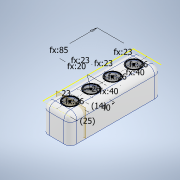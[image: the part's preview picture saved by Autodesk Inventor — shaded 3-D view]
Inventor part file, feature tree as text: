
AUTODESK INVENTOR PART (.ipt)
format: ipt  version: 2021 (Build 250183000, 183)  size: 2,222,592 bytes
history: native  units: in
note: dims shown in document units (in); Inventor stores cm internally (conversion verified against a paired STEP export)
features: extrude x9, other x9, fillet x2
ambient origin geometry x8: Origin, YZ Plane, XZ Plane, XY Plane, X Axis, Y Axis, Z Axis, Center Point
bodies: Body1 (feature_tree)
feature tree (20):
  extrude  "Base"  Depth=6.6929in
  other  "Top Indent Sketch"
  extrude  "Top"  Depth=2.0472in
  extrude  "Walls"  Depth=1.9685in TaperAngle=0.0deg
  fillet  "Outer"  Radius=1.0236in
  extrude  "Outer Wire"  Depth=1.0236in
  extrude  "Wall Holes"  Depth=1.0236in
  extrude  "Text"  Depth=1.0236in
  extrude  "Inner Sketch"  Depth=1.5748in
  fillet  "Inner Fillet"  Radius=1.5748in
  extrude  "Top Indent"  Depth=1.5748in
  other  "Wire Hole Plane"
  extrude  "Wire Hole"  Depth=0.7087in TaperAngle=0.0deg
  other  "Base Sketch"
  other  "Walls Sketch"
  other  "Outer Wire Sketch"
  other  "Wall Holes Sketch"
  other  "Text Sketch"
  other  "Inner Support Sketch"
  other  "Wire Hole Sketch"
